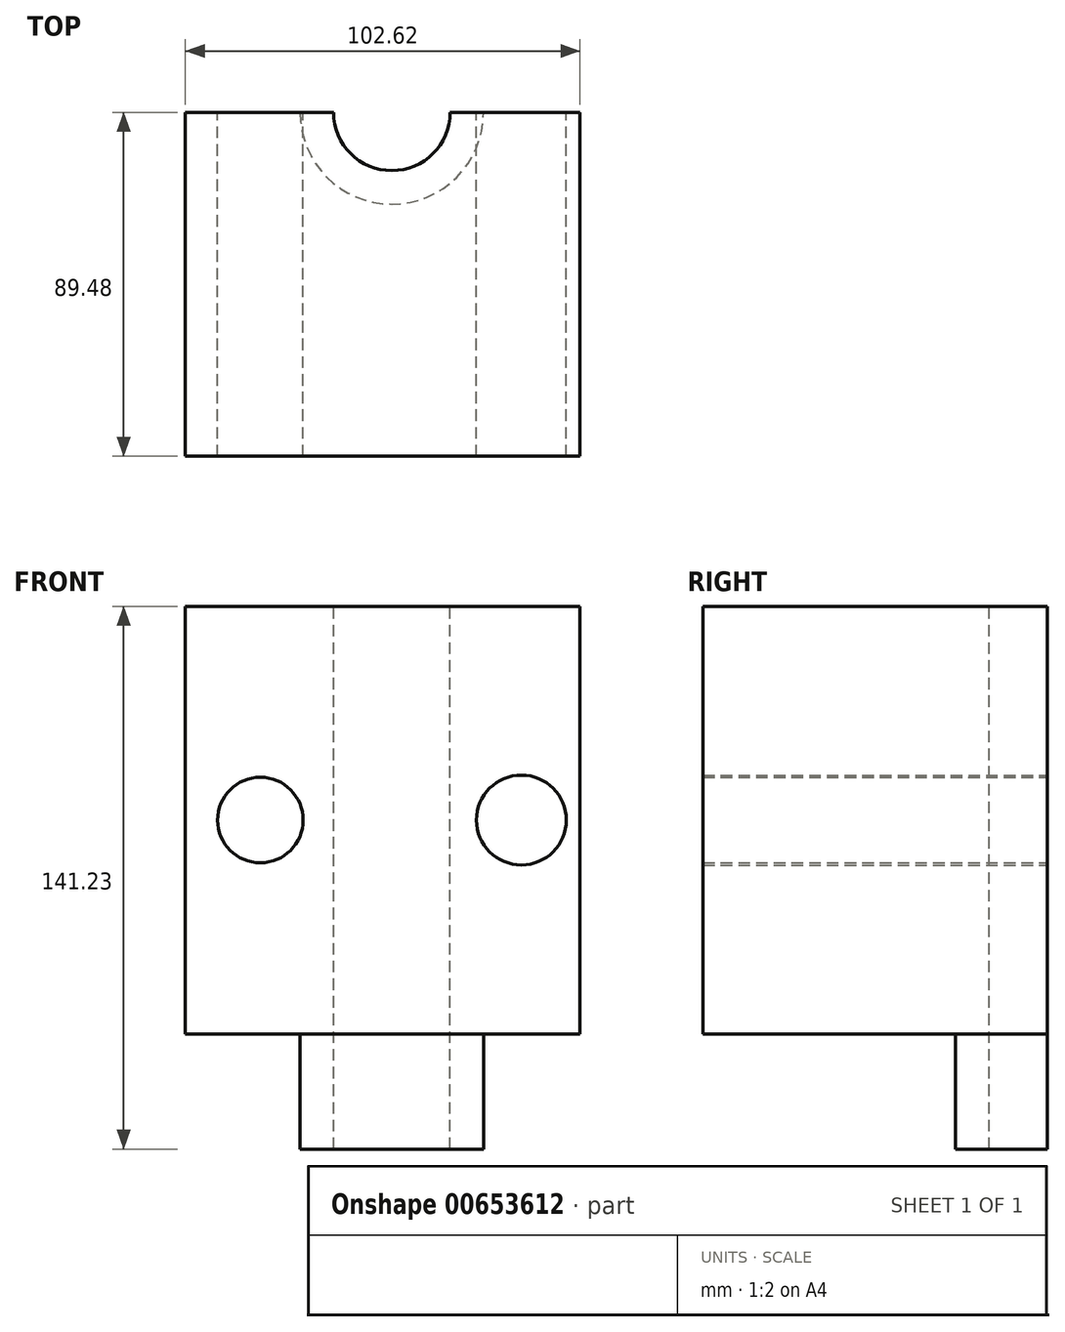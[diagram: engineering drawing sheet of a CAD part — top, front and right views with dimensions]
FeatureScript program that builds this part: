
annotation { "Feature Type Name" : "Feature", "Feature Type Description" : "" }
export const myFeature = defineFeature(function(context is Context, id is Id, definition is map)
    precondition{}
    {
        {
            var Q0;
            Q0=qCreatedBy(makeId("Top.planeOp"),FACE);
            var sketch = newSketch(context, id + "F0", { "sketchPlane" : qUnion([Q0])});
            skLineSegment(sketch, "E0", {"start": v(-60.31, 45.96) * mm, "end": v(-60.31, -43.52) * mm});
            skLineSegment(sketch, "E1", {"start": v(-60.31, -43.52) * mm, "end": v(42.31, -43.52) * mm});
            skLineSegment(sketch, "E2", {"start": v(42.31, -43.52) * mm, "end": v(42.31, 45.96) * mm});
            skLineSegment(sketch, "E3", {"start": v(42.31, 45.96) * mm, "end": v(-60.31, 45.96) * mm});
            skSolve(sketch);
        }
        {
            var Q0;
            Q0 = qSketchRegion(id + "F0", true);
            extrude(context, id + "F1", {"entities" : qUnion([Q0]), "endBound" : BoundingType.SYMMETRIC, "depth" : 111.25 * mm, "offsetDistance" : 25.4 * mm});
        }
        {
            var Q0;
            Q0=makeQuery(id+"F1.opExtrude","CAP_FACE",FACE,{"disambiguationData":[OSD([sQuery(id+"F0.wireOp",EDGE,"E0"),sQuery(id+"F0.wireOp",EDGE,"E1"),sQuery(id+"F0.wireOp",EDGE,"E2"),sQuery(id+"F0.wireOp",EDGE,"E3")])],"isStart":false});
            var sketch = newSketch(context, id + "F2", { "sketchPlane" : qUnion([Q0])});
            skCircle(sketch, "E4", {"center": v(-6.62, 45.96) * mm, "radius": 23.85 * mm});
            skCircle(sketch, "E5", {"center": v(-6.62, 45.96) * mm, "radius": 15.14 * mm});
            skSolve(sketch);
        }
        {
            var Q0;
            {var subQ0=sQuery(id+"F2.wireOp",EDGE,"E4");var subQ1=makeQuery(id+"F1.opExtrude","CAP_EDGE",EDGE,{"disambiguationData":[OSD([sQuery(id+"F0.wireOp",EDGE,"E3")])],"isStart":false});var subQ2=makeQuery(id+"F2.imprint","INTERSECT",VERTEX,{"disambiguationData":[OD(0.0)],"derivedFrom":[subQ1,subQ0]});Q0=makeQuery(id+"F2.imprint","IMPRINT",FACE,{"disambiguationData":[TD([[makeQuery(id+"F2.imprint","IMPRINT",EDGE,{"disambiguationData":[TD([[subQ2,-1.0]])],"derivedFrom":subQ0}),1.0]])]});}
            extrude(context, id + "F3", {"entities" : qUnion([Q0]), "operationType" : NewBodyOperationType.ADD, "oppositeDirection" : true, "depth" : 141.22 * mm, "offsetDistance" : 25.4 * mm});
        }
        {
            var Q0;
            {var subQ0=sQuery(id+"F0.wireOp",EDGE,"E3");var subQ3=sQuery(id+"F2.wireOp",EDGE,"E5");Q0=makeQuery(id+"F3.boolean.opBoolean","SPLIT",FACE,{"disambiguationData":[TD([makeQuery(id+"F3.opExtrude","SWEPT_FACE",FACE,{"disambiguationData":[OSD([subQ3])]})])],"derivedFrom":makeQuery(id+"F1.opExtrude","CAP_FACE",FACE,{"disambiguationData":[OSD([sQuery(id+"F0.wireOp",EDGE,"E0"),sQuery(id+"F0.wireOp",EDGE,"E1"),sQuery(id+"F0.wireOp",EDGE,"E2"),subQ0])],"isStart":true})});}
            extrude(context, id + "F4", {"entities" : qUnion([Q0]), "operationType" : NewBodyOperationType.REMOVE, "oppositeDirection" : true, "depth" : 156.72 * mm, "offsetDistance" : 25.4 * mm});
        }
        {
            var Q0;
            {var subQ0=sQuery(id+"F0.wireOp",EDGE,"E2");var subQ1=sQuery(id+"F2.wireOp",EDGE,"E4");var subQ2=sQuery(id+"F0.wireOp",EDGE,"E3");var subQ6=makeQuery(id+"F1.opExtrude","CAP_EDGE",EDGE,{"disambiguationData":[OSD([subQ2])],"isStart":false});Q0=makeQuery(id+"F4.boolean.opBoolean","SPLIT",FACE,{"disambiguationData":[TD([makeQuery(id+"F1.opExtrude","SWEPT_FACE",FACE,{"disambiguationData":[OSD([subQ0])]})])],"derivedFrom":makeQuery(id+"F3.boolean.opBoolean","MERGE",FACE,{"derivedFrom":[makeQuery(id+"F1.opExtrude","SWEPT_FACE",FACE,{"disambiguationData":[OSD([subQ2])]}),makeQuery(id+"F3.opExtrude","SWEPT_FACE",FACE,{"disambiguationData":[OSD([subQ2]),TDD([makeQuery(id+"F2.imprint","IMPRINT",EDGE,{"disambiguationData":[TD([[makeQuery(id+"F2.imprint","INTERSECT",VERTEX,{"disambiguationData":[OD(0.0)],"derivedFrom":[subQ6,subQ1]}),1.0]])],"derivedFrom":subQ6})])]}),makeQuery(id+"F3.opExtrude","SWEPT_FACE",FACE,{"disambiguationData":[OSD([subQ2]),TDD([makeQuery(id+"F2.imprint","IMPRINT",EDGE,{"disambiguationData":[TD([[makeQuery(id+"F2.imprint","INTERSECT",VERTEX,{"disambiguationData":[OD(1.0)],"derivedFrom":[subQ6,subQ1]}),-1.0]])],"derivedFrom":subQ6})])]})]})});}
            var sketch = newSketch(context, id + "F5", { "sketchPlane" : qUnion([Q0])});
            skCircle(sketch, "E6", {"center": v(-27.07, 0) * mm, "radius": 11.69 * mm});
            skCircle(sketch, "E7", {"center": v(43.28, 0) * mm, "radius": 11.08 * mm});
            skSolve(sketch);
        }
        {
            var Q0;
            Q0=makeQuery(id+"F5.imprint","IMPRINT",FACE,{"disambiguationData":[TD([[makeQuery(id+"F5.imprint","IMPRINT",EDGE,{"derivedFrom":sQuery(id+"F5.wireOp",EDGE,"E6")}),1.0]])]});
            extrude(context, id + "F6", {"entities" : qUnion([Q0]), "operationType" : NewBodyOperationType.REMOVE, "endBound" : BoundingType.SYMMETRIC, "oppositeDirection" : true, "depth" : 269.75 * mm, "offsetDistance" : 25.4 * mm});
        }
        {
            var Q0;
            {var subQ0=sQuery(id+"F2.wireOp",EDGE,"E4");var subQ1=sQuery(id+"F0.wireOp",EDGE,"E3");var subQ4=sQuery(id+"F0.wireOp",EDGE,"E0");var subQ6=makeQuery(id+"F1.opExtrude","CAP_EDGE",EDGE,{"disambiguationData":[OSD([subQ1])],"isStart":false});Q0=makeQuery(id+"F4.boolean.opBoolean","SPLIT",FACE,{"disambiguationData":[TD([makeQuery(id+"F1.opExtrude","SWEPT_FACE",FACE,{"disambiguationData":[OSD([subQ4])]})])],"derivedFrom":makeQuery(id+"F3.boolean.opBoolean","MERGE",FACE,{"derivedFrom":[makeQuery(id+"F1.opExtrude","SWEPT_FACE",FACE,{"disambiguationData":[OSD([subQ1])]}),makeQuery(id+"F3.opExtrude","SWEPT_FACE",FACE,{"disambiguationData":[OSD([subQ1]),TDD([makeQuery(id+"F2.imprint","IMPRINT",EDGE,{"disambiguationData":[TD([[makeQuery(id+"F2.imprint","INTERSECT",VERTEX,{"disambiguationData":[OD(0.0)],"derivedFrom":[subQ6,subQ0]}),1.0]])],"derivedFrom":subQ6})])]}),makeQuery(id+"F3.opExtrude","SWEPT_FACE",FACE,{"disambiguationData":[OSD([subQ1]),TDD([makeQuery(id+"F2.imprint","IMPRINT",EDGE,{"disambiguationData":[TD([[makeQuery(id+"F2.imprint","INTERSECT",VERTEX,{"disambiguationData":[OD(1.0)],"derivedFrom":[subQ6,subQ0]}),-1.0]])],"derivedFrom":subQ6})])]})]})});}
            var sketch = newSketch(context, id + "F7", { "sketchPlane" : qUnion([Q0])});
            skCircle(sketch, "E8", {"center": v(40.8, 0) * mm, "radius": 11.13 * mm});
            skSolve(sketch);
        }
        {
            var Q0;
            Q0 = qSketchRegion(id + "F7", true);
            extrude(context, id + "F8", {"entities" : qUnion([Q0]), "operationType" : NewBodyOperationType.REMOVE, "oppositeDirection" : true, "depth" : 268.48 * mm, "offsetDistance" : 25.4 * mm});
        }
    });
